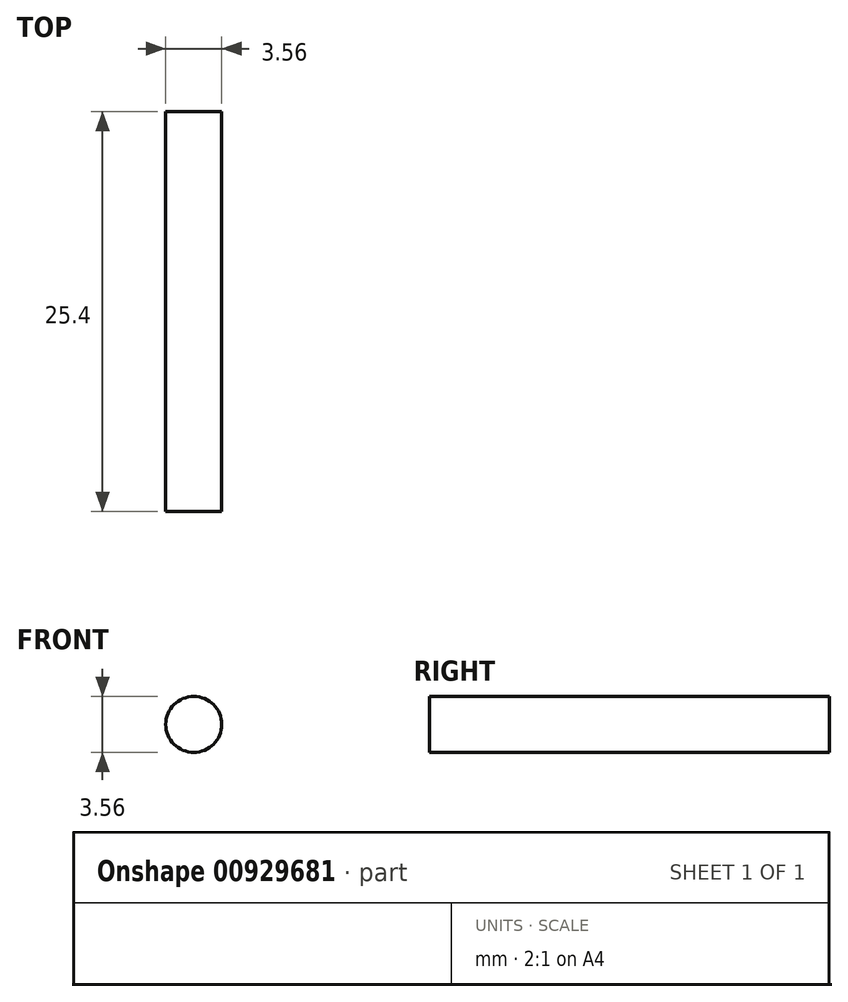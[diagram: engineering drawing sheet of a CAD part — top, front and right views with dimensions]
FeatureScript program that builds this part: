
annotation { "Feature Type Name" : "Feature", "Feature Type Description" : "" }
export const myFeature = defineFeature(function(context is Context, id is Id, definition is map)
    precondition{}
    {
        {
            var Q0;
            Q0=qCreatedBy(makeId("Front.planeOp"),FACE);
            var sketch = newSketch(context, id + "F0", { "sketchPlane" : qUnion([Q0])});
            skCircle(sketch, "E0", {"center": v(0, 0) * mm, "radius": 1.78 * mm});
            skSolve(sketch);
        }
        {
            var Q0;
            Q0 = qSketchRegion(id + "F0", true);
            extrude(context, id + "F1", {"entities" : qUnion([Q0]), "depth" : 25.4 * mm, "offsetDistance" : 25.4 * mm});
        }
    });
